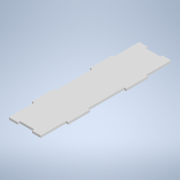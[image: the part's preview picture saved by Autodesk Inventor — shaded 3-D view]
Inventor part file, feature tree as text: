
AUTODESK INVENTOR PART (.ipt)
format: ipt  version: 2020.3 (Build 243373000, 373)  size: 142,848 bytes
history: native  units: mm
features: extrude x2, sketch x2
ambient origin geometry x8: Origin, YZ Plane, XZ Plane, XY Plane, X Axis, Y Axis, Z Axis, Center Point
bodies: Solid1 (feature_tree)
feature tree (4):
  extrude  "Base"  Depth=50.0mm
  extrude  "Tabs"  Depth=35.0mm
  sketch  "Sketch1"  dims[d0=180.0mm d1=50.0mm]
  sketch  "Sketch2"  dims[d2=3.0mm d3=0.0mm d10=35.0mm d11=35.0mm d12=30.0mm d13=30.0mm d14=50.0mm d15=3.0mm d16=0.0mm d17=0.0mm d18=20.0mm d19=10.0mm d20=3.0mm]
